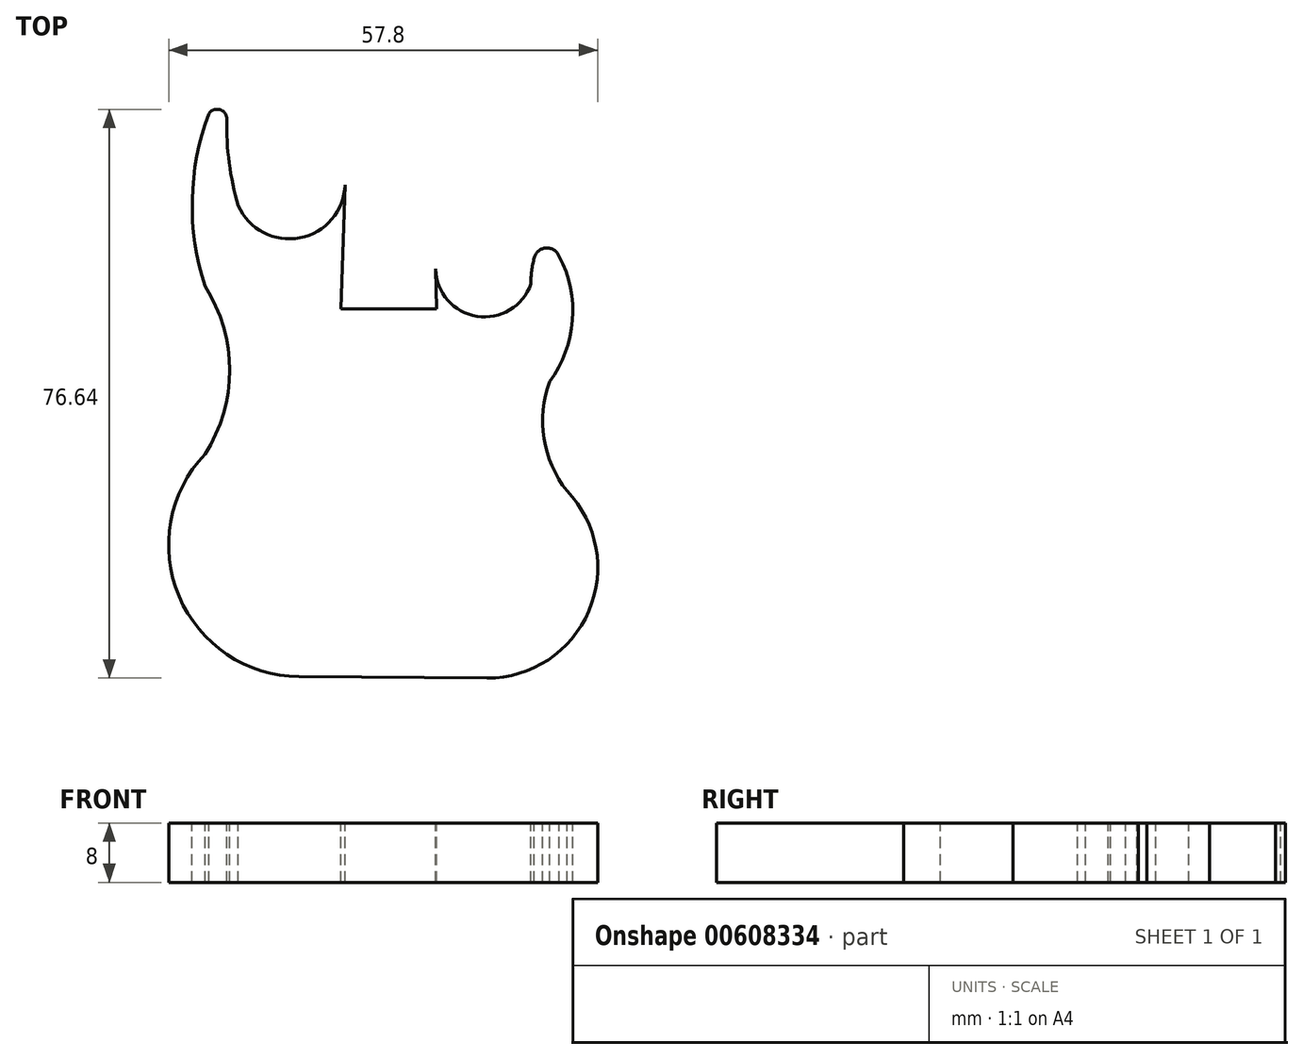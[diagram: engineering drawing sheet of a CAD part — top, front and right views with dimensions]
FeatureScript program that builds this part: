
annotation { "Feature Type Name" : "Feature", "Feature Type Description" : "" }
export const myFeature = defineFeature(function(context is Context, id is Id, definition is map)
    precondition{}
    {
        {
            var Q0;
            Q0=qCreatedBy(makeId("Top.planeOp"),FACE);
            var sketch = newSketch(context, id + "F0", { "sketchPlane" : qUnion([Q0])});
            skPoint(sketch, "E0.middle", {"position": v(0, 0) * mm});
            skArc(sketch, "E1", {"start": v(-24.76, 38.02) * mm, "mid": v(-26.98, 26.44) * mm, "end": v(-25.27, 14.79) * mm});
            skArc(sketch, "E2", {"start": v(-25.27, -7.86) * mm, "mid": v(-28.75, -27) * mm, "end": v(-12.6, -37.82) * mm});
            skArc(sketch, "E3", {"start": v(-25.27, -7.86) * mm, "mid": v(-21.94, 3.46) * mm, "end": v(-25.27, 14.79) * mm});
            skArc(sketch, "E4", {"start": v(-22.32, 37.28) * mm, "mid": v(-23.26, 38.56) * mm, "end": v(-24.76, 38.02) * mm});
            skArc(sketch, "E5", {"start": v(-22.32, 37.28) * mm, "mid": v(-22, 31.4) * mm, "end": v(-20.79, 25.64) * mm});
            skArc(sketch, "E6", {"start": v(-20.79, 25.64) * mm, "mid": v(-12.24, 21.35) * mm, "end": v(-6.4, 28.92) * mm});
            skArc(sketch, "E7", {"start": v(5.81, 17.57) * mm, "mid": v(11.15, 10.77) * mm, "end": v(18.64, 15.08) * mm});
            skArc(sketch, "E8", {"start": v(21.15, 1.93) * mm, "mid": v(24.25, 10.18) * mm, "end": v(22.46, 18.8) * mm});
            skArc(sketch, "E9", {"start": v(21.15, 1.93) * mm, "mid": v(20.4, -5.74) * mm, "end": v(23.51, -12.8) * mm});
            skArc(sketch, "E10", {"start": v(12.75, -38.02) * mm, "mid": v(26.45, -28.96) * mm, "end": v(23.51, -12.8) * mm});
            skLineSegment(sketch, "E11", {"start": v(-12.6, -37.82) * mm, "end": v(12.75, -38.02) * mm});
            skLineSegment(sketch, "E12", {"start": v(-4, 98.38) * mm, "end": v(-6.97, 11.73) * mm});
            skLineSegment(sketch, "E13", {"start": v(4, 98.38) * mm, "end": v(5.93, 11.73) * mm});
            skArc(sketch, "E14", {"start": v(22.46, 18.8) * mm, "mid": v(20.71, 19.94) * mm, "end": v(19.1, 18.61) * mm});
            skArc(sketch, "E15", {"start": v(19.1, 18.61) * mm, "mid": v(18.75, 16.86) * mm, "end": v(18.64, 15.08) * mm});
            skArc(sketch, "E16", {"start": v(-4, 98.38) * mm, "mid": v(-5.5, 102.93) * mm, "end": v(-9.58, 105.42) * mm});
            skLineSegment(sketch, "E17", {"start": v(-9.58, 105.42) * mm, "end": v(6.53, 131.12) * mm});
            skLineSegment(sketch, "E18", {"start": v(6.53, 131.12) * mm, "end": v(8.93, 125.76) * mm});
            skArc(sketch, "E19", {"start": v(8.93, 125.76) * mm, "mid": v(5.09, 112.32) * mm, "end": v(4, 98.38) * mm});
            skLineSegment(sketch, "E20", {"start": v(-6.97, 11.73) * mm, "end": v(5.93, 11.73) * mm});
            skLineSegment(sketch, "E21", {"start": v(-4, 98.38) * mm, "end": v(4, 98.38) * mm});
            skSolve(sketch);
        }
        {
            var Q0;
            Q0=makeQuery(id+"F0.imprint","IMPRINT",FACE,{"disambiguationData":[TD([[makeQuery(id+"F0.imprint","IMPRINT",EDGE,{"derivedFrom":sQuery(id+"F0.wireOp",EDGE,"E1")}),1.0]])]});
            extrude(context, id + "F1", {"entities" : qUnion([Q0]), "depth" : -8 * mm, "offsetDistance" : 25 * mm});
        }
    });
